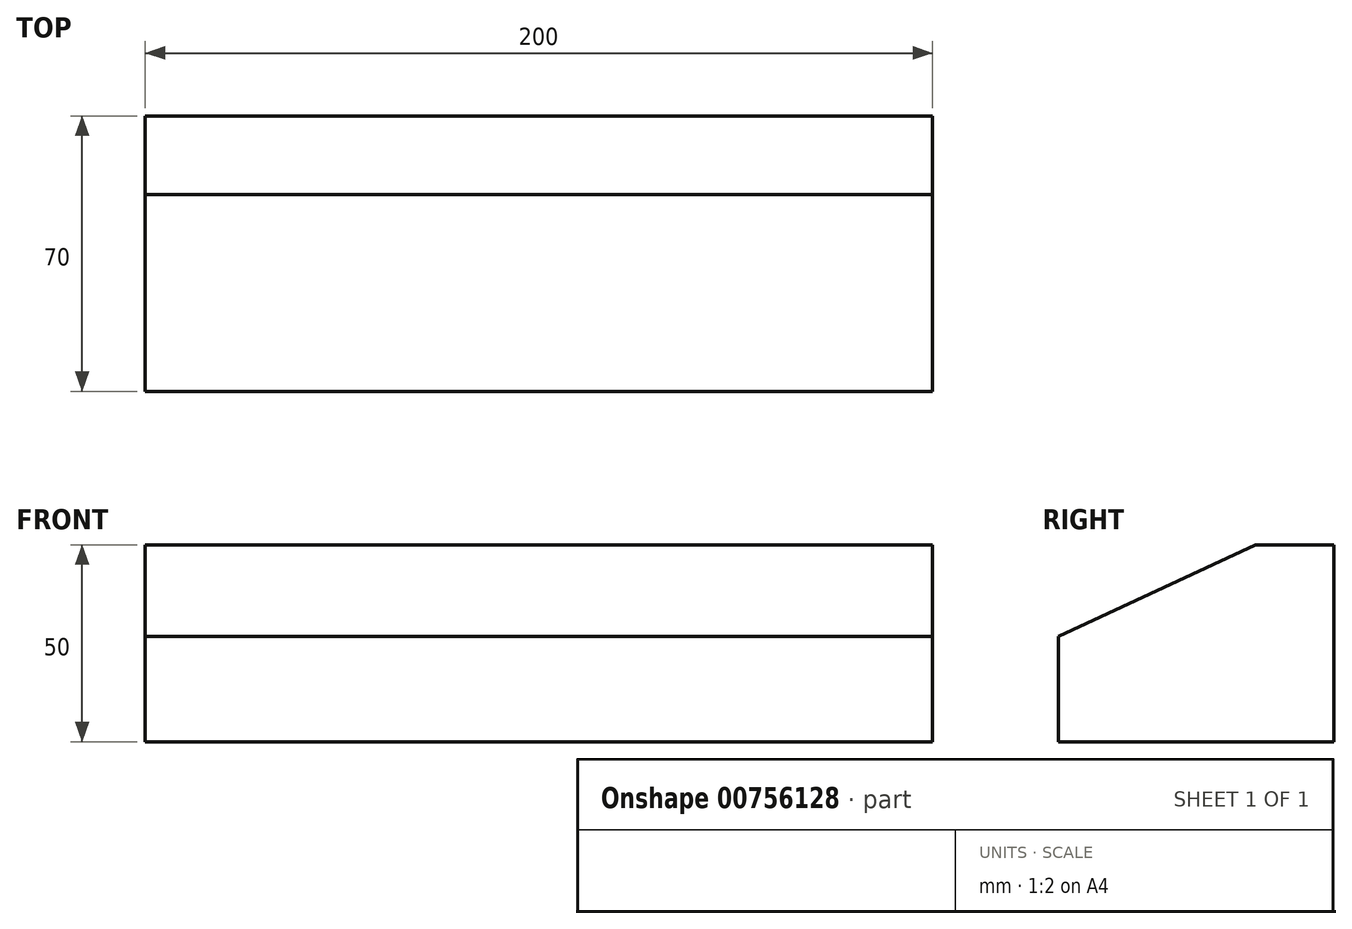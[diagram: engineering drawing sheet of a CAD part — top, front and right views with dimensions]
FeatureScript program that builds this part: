
annotation { "Feature Type Name" : "Feature", "Feature Type Description" : "" }
export const myFeature = defineFeature(function(context is Context, id is Id, definition is map)
    precondition{}
    {
        {
            var Q0;
            Q0=qCreatedBy(makeId("Top.planeOp"),FACE);
            var sketch = newSketch(context, id + "F0", { "sketchPlane" : qUnion([Q0])});
            skLineSegment(sketch, "E0.bottom", {"start": v(-100, -35) * mm, "end": v(100, -35) * mm});
            skLineSegment(sketch, "E0.top", {"start": v(-100, 35) * mm, "end": v(100, 35) * mm});
            skLineSegment(sketch, "E0.left", {"start": v(-100, -35) * mm, "end": v(-100, 35) * mm});
            skLineSegment(sketch, "E0.right", {"start": v(100, -35) * mm, "end": v(100, 35) * mm});
            skPoint(sketch, "E0.middle", {"position": v(0, 0) * mm});
            skSolve(sketch);
        }
        {
            var Q0;
            Q0=makeQuery(id+"F0.imprint","IMPRINT",FACE,{"disambiguationData":[TD([[makeQuery(id+"F0.imprint","IMPRINT",EDGE,{"derivedFrom":sQuery(id+"F0.wireOp",EDGE,"E0.bottom")}),1.0]])]});
            extrude(context, id + "F1", {"entities" : qUnion([Q0]), "depth" : 50 * mm, "offsetDistance" : 25 * mm});
        }
        {
            var Q0;
            Q0=makeQuery(id+"F1.opExtrude","CAP_EDGE",EDGE,{"disambiguationData":[OSD([sQuery(id+"F0.wireOp",EDGE,"E0.bottom")])],"isStart":false});
            chamfer(context, id + "F2", {"entities" : qUnion([Q0]), "chamferType" : ChamferType.OFFSET_ANGLE, "width" : 50 * mm, "oppositeDirection" : false, "angle" : 25 * degree, "tangentPropagation" : true});
        }
    });
